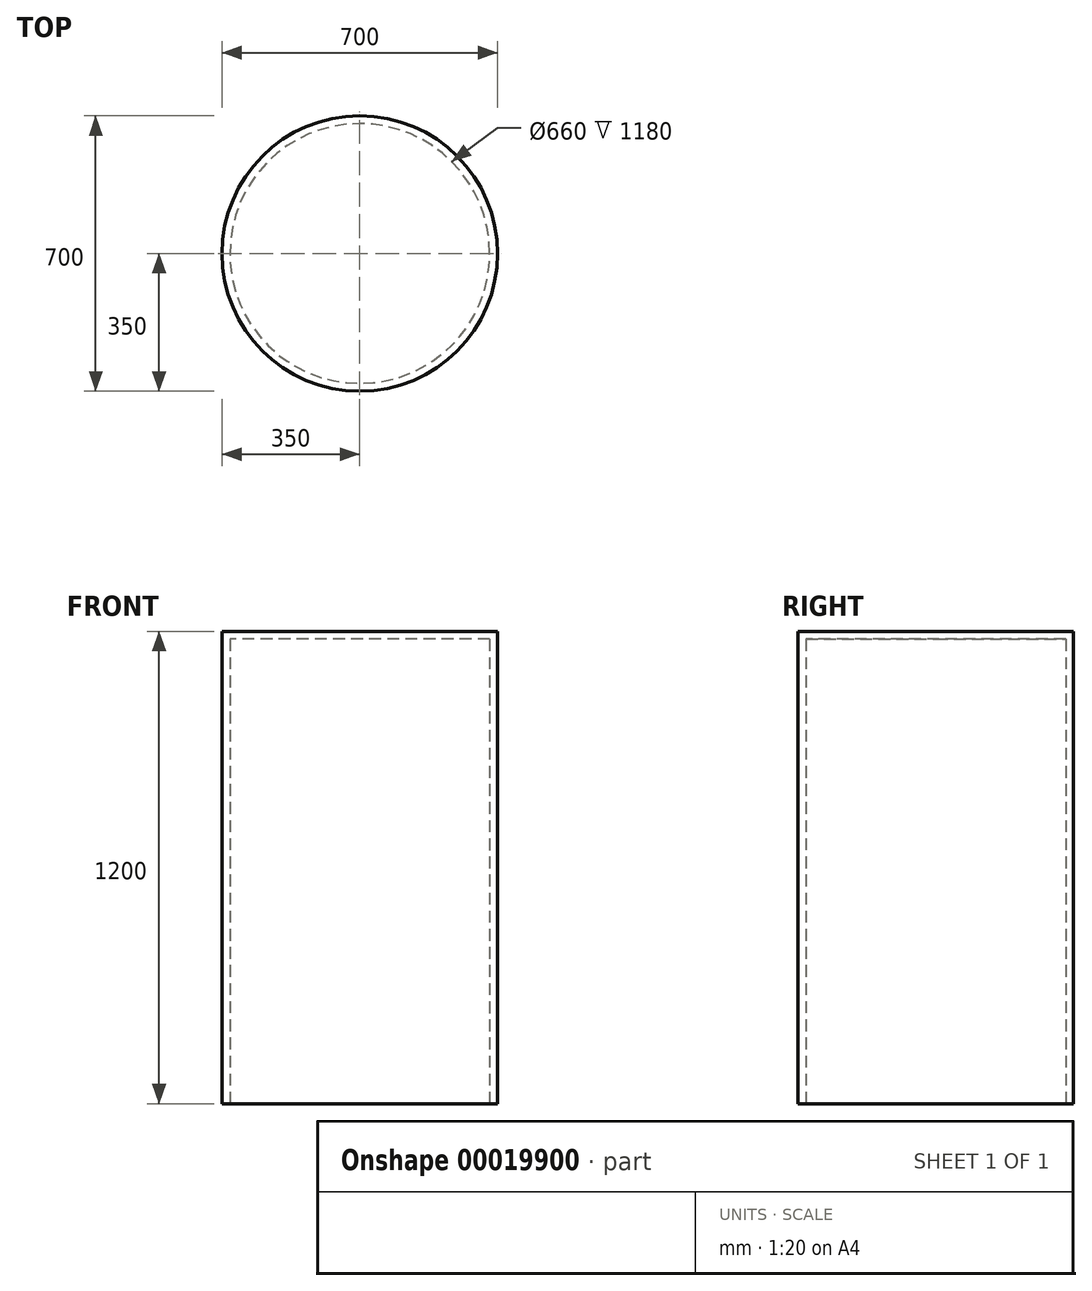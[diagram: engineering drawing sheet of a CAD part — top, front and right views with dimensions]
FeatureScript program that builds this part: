
annotation { "Feature Type Name" : "Feature", "Feature Type Description" : "" }
export const myFeature = defineFeature(function(context is Context, id is Id, definition is map)
    precondition{}
    {
        {
            var Q0;
            Q0=qCreatedBy(makeId("Top.planeOp"),FACE);
            var sketch = newSketch(context, id + "F0", { "sketchPlane" : qUnion([Q0])});
            skCircle(sketch, "E0", {"center": v(0, 0) * mm, "radius": 350 * mm});
            skSolve(sketch);
        }
        {
            var Q0;
            Q0=makeQuery(id+"F0.imprint","IMPRINT",FACE,{"disambiguationData":[TD([[makeQuery(id+"F0.imprint","IMPRINT",EDGE,{"derivedFrom":sQuery(id+"F0.wireOp",EDGE,"E0")}),1.0]])]});
            extrude(context, id + "F1", {"entities" : qUnion([Q0]), "depth" : 1200 * mm});
        }
        {
            var Q0;
            Q0=makeQuery(id+"F1.opExtrude","CAP_FACE",FACE,{"disambiguationData":[OSD([sQuery(id+"F0.wireOp",EDGE,"E0")])],"isStart":true});
            shell(context, id + "F2", {"entities" : qUnion([Q0]), "thickness" : 20 * mm});
        }
    });
